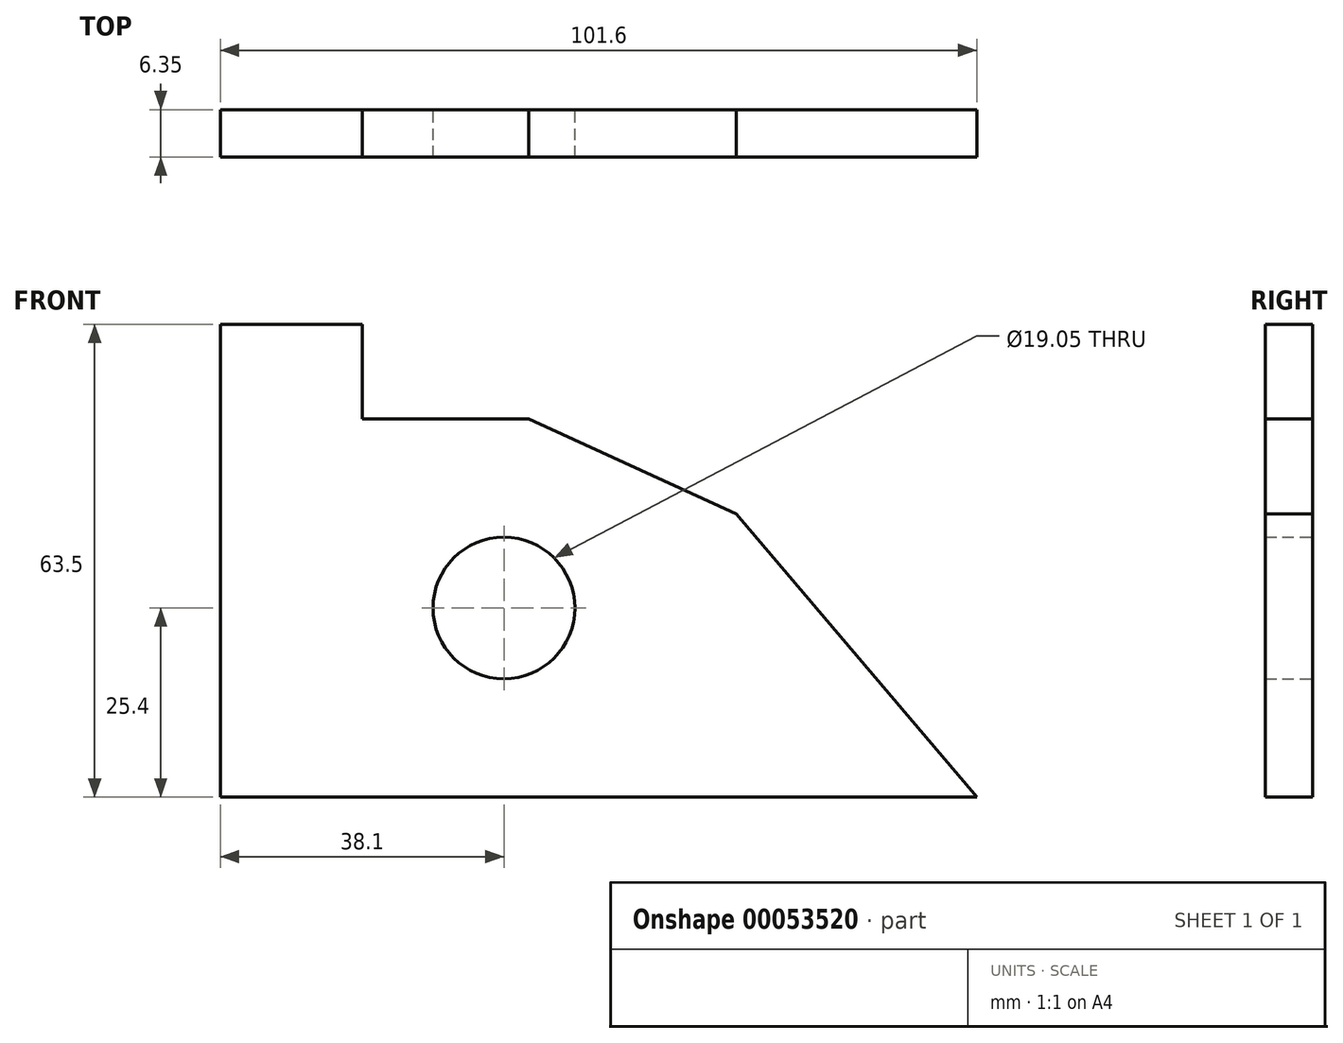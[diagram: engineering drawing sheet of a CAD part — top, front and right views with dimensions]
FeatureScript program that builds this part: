
annotation { "Feature Type Name" : "Feature", "Feature Type Description" : "" }
export const myFeature = defineFeature(function(context is Context, id is Id, definition is map)
    precondition{}
    {
        {
            var Q0;
            Q0=qCreatedBy(makeId("Front.planeOp"),FACE);
            var sketch = newSketch(context, id + "F0", { "sketchPlane" : qUnion([Q0])});
            skCircle(sketch, "E0", {"center": v(0, 0) * mm, "radius": 9.53 * mm});
            skLineSegment(sketch, "E1", {"start": v(-38.1, -25.4) * mm, "end": v(63.5, -25.4) * mm});
            skLineSegment(sketch, "E2", {"start": v(-38.1, -25.4) * mm, "end": v(-38.1, 38.1) * mm});
            skLineSegment(sketch, "E3", {"start": v(-38.1, 38.1) * mm, "end": v(-19.05, 38.1) * mm});
            skLineSegment(sketch, "E4", {"start": v(-19.05, 25.4) * mm, "end": v(-19.05, 38.1) * mm});
            skLineSegment(sketch, "E5", {"start": v(-19.05, 25.4) * mm, "end": v(3.3, 25.4) * mm});
            skLineSegment(sketch, "E6", {"start": v(3.3, 25.4) * mm, "end": v(31.18, 12.62) * mm});
            skLineSegment(sketch, "E7", {"start": v(31.18, 12.62) * mm, "end": v(63.5, -25.4) * mm});
            skSolve(sketch);
        }
        {
            var Q0;
            Q0 = qSketchRegion(id + "F0", true);
            extrude(context, id + "F1", {"entities" : qUnion([Q0]), "depth" : 6.35 * mm});
        }
    });
